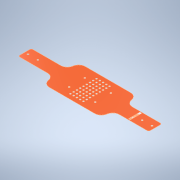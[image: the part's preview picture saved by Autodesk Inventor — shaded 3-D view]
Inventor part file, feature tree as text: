
AUTODESK INVENTOR PART (.ipt)
format: ipt  version: 2022 (Build 260153000, 153)  size: 418,816 bytes
history: native  units: in
note: dims shown in document units (in); Inventor stores cm internally (conversion verified against a paired STEP export)
features: sketch x5, extrude x2, hole x2, emboss x1
ambient origin geometry x8: Origin, YZ Plane, XZ Plane, XY Plane, X Axis, Y Axis, Z Axis, Center Point
bodies: Solid1 (feature_tree)
feature tree (10):
  extrude  "Extrusion1"  Depth=1.378in
  hole  "Hole1"  [1 undecoded]
  hole  "Hole2"  [1 undecoded]
  extrude  "Extrusion2"  Depth=0.25in
  emboss  "Emboss1"
  sketch  "Sketch1"  dims[d0=2.2441in d1=1.378in]
  sketch  "Sketch2"  dims[d2=1.378in d3=0.5in]
  sketch  "Sketch3"  dims[d4=0.25in d5=0.25in]
  sketch  "Sketch4"  dims[d6=0.25in d7=0.25in]
  sketch  "Sketch5"  dims[d8=0.25in d9=0.25in d10=0.25in d11=0.0047in d12=0.0in d13=0.0625in d14=0.5in d15=0.5in d16=0.064in d17=0.75in d18=0.217in d19=0.25in d20=90.0deg d21=1.0in d22=0.8108in d23=0.125in d24=0.125in d25=0.5in d26=0.25in d27=3.5433in d29=0.125in d30=1.9685in d32=0.125in d35=0.0625in d36=0.75in d37=0.375in d38=0.25in d39=0.5635in d40=1.0in d41=0.8108in d42=0.002in d43=0.0in d44=0.002in d45=0.0in d46=2.0in d47=2.0in d48=0.3in d49=0.3in]
note: 2 required parameter values undecoded (feature->parameter linkage not recoverable at this tier; creation-order binding heuristic only, values carry confidence <= 0.55)
